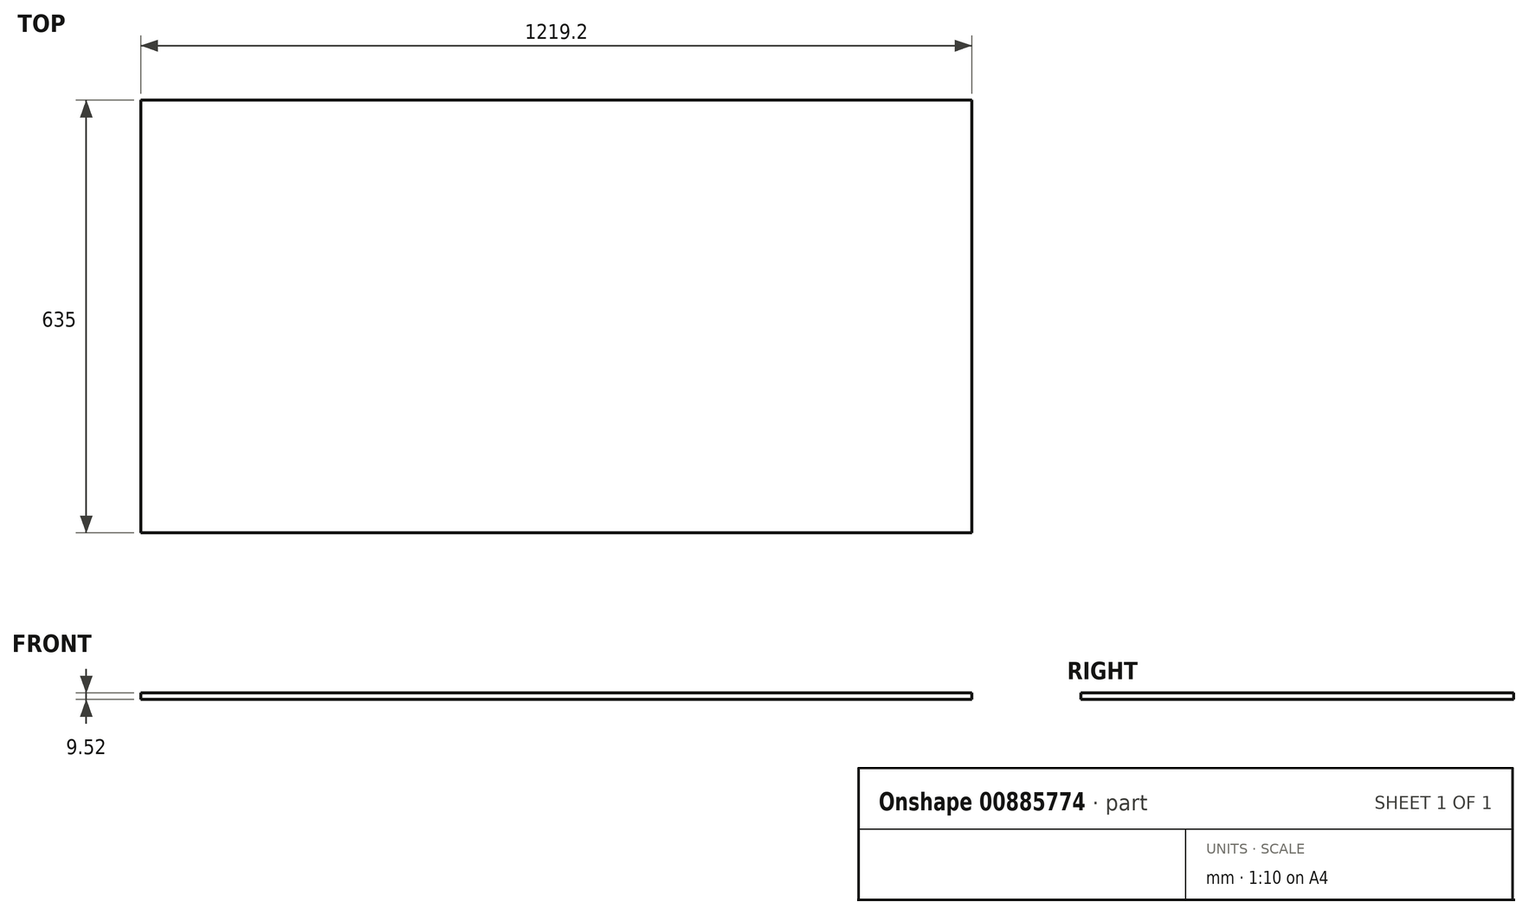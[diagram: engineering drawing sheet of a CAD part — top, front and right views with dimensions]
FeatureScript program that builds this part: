
annotation { "Feature Type Name" : "Feature", "Feature Type Description" : "" }
export const myFeature = defineFeature(function(context is Context, id is Id, definition is map)
    precondition{}
    {
        {
            var Q0;
            Q0=qCreatedBy(makeId("Top.planeOp"),FACE);
            var sketch = newSketch(context, id + "F0", { "sketchPlane" : qUnion([Q0])});
            skLineSegment(sketch, "E0.bottom", {"start": v(609.6, -317.5) * mm, "end": v(-609.6, -317.5) * mm});
            skLineSegment(sketch, "E0.top", {"start": v(609.6, 317.5) * mm, "end": v(-609.6, 317.5) * mm});
            skLineSegment(sketch, "E0.left", {"start": v(609.6, -317.5) * mm, "end": v(609.6, 317.5) * mm});
            skLineSegment(sketch, "E0.right", {"start": v(-609.6, -317.5) * mm, "end": v(-609.6, 317.5) * mm});
            skPoint(sketch, "E0.middle", {"position": v(0, 0) * mm});
            skSolve(sketch);
        }
        {
            var Q0;
            Q0=makeQuery(id+"F0.imprint","IMPRINT",FACE,{"disambiguationData":[TD([[makeQuery(id+"F0.imprint","IMPRINT",EDGE,{"derivedFrom":sQuery(id+"F0.wireOp",EDGE,"E0.bottom")}),-1.0]])]});
            extrude(context, id + "F1", {"entities" : qUnion([Q0]), "endBound" : BoundingType.SYMMETRIC, "depth" : 9.52 * mm, "offsetDistance" : 25.4 * mm});
        }
    });
